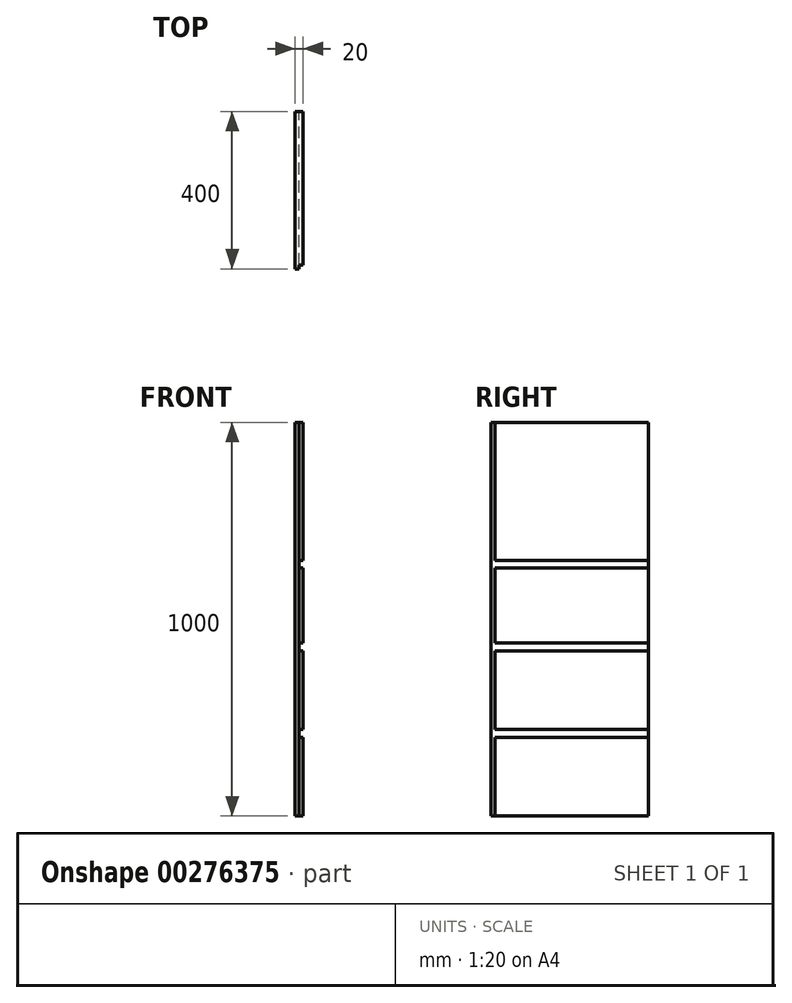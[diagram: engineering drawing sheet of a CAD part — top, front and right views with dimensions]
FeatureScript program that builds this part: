
annotation { "Feature Type Name" : "Feature", "Feature Type Description" : "" }
export const myFeature = defineFeature(function(context is Context, id is Id, definition is map)
    precondition{}
    {
        {
            var Q0;
            Q0=qCreatedBy(makeId("Right.planeOp"),FACE);
            var sketch = newSketch(context, id + "F0", { "sketchPlane" : qUnion([Q0])});
            skLineSegment(sketch, "E0.bottom", {"start": v(-298.33, 493.15) * mm, "end": v(101.67, 493.15) * mm});
            skLineSegment(sketch, "E0.top", {"start": v(-298.33, -506.85) * mm, "end": v(101.67, -506.85) * mm});
            skLineSegment(sketch, "E0.left", {"start": v(-298.33, 493.15) * mm, "end": v(-298.33, -506.85) * mm});
            skLineSegment(sketch, "E0.right", {"start": v(101.67, 493.15) * mm, "end": v(101.67, -506.85) * mm});
            skLineSegment(sketch, "E1", {"start": v(-288.33, 493.15) * mm, "end": v(-288.33, -506.85) * mm});
            skLineSegment(sketch, "E2", {"start": v(-298.33, 143.15) * mm, "end": v(101.67, 143.15) * mm});
            skLineSegment(sketch, "E3", {"start": v(-298.33, 123.15) * mm, "end": v(101.67, 123.15) * mm});
            skLineSegment(sketch, "E4", {"start": v(-298.33, -66.85) * mm, "end": v(101.67, -66.85) * mm});
            skLineSegment(sketch, "E5", {"start": v(-298.33, -86.85) * mm, "end": v(105.13, -86.85) * mm});
            skLineSegment(sketch, "E6", {"start": v(-298.33, -286.85) * mm, "end": v(101.67, -286.85) * mm});
            skLineSegment(sketch, "E7", {"start": v(-298.33, -306.85) * mm, "end": v(101.67, -306.85) * mm});
            skSolve(sketch);
        }
        {
            var Q0;
            {var subQ0=sQuery(id+"F0.wireOp",EDGE,"E0.left");var subQ1=sQuery(id+"F0.wireOp",EDGE,"E0.bottom");var subQ2=makeQuery(id+"F0.imprint","INTERSECT",VERTEX,{"derivedFrom":[subQ1,subQ0]});Q0=makeQuery(id+"F0.imprint","IMPRINT",FACE,{"disambiguationData":[TD([[makeQuery(id+"F0.imprint","IMPRINT",EDGE,{"disambiguationData":[TD([[subQ2,-1.0]])],"derivedFrom":subQ1}),-1.0]])]});}
            var Q1;
            {var subQ0=sQuery(id+"F0.wireOp",EDGE,"E2");var subQ1=sQuery(id+"F0.wireOp",EDGE,"E0.left");var subQ2=makeQuery(id+"F0.imprint","INTERSECT",VERTEX,{"derivedFrom":[subQ1,subQ0]});Q1=makeQuery(id+"F0.imprint","IMPRINT",FACE,{"disambiguationData":[TD([[makeQuery(id+"F0.imprint","IMPRINT",EDGE,{"disambiguationData":[TD([[subQ2,-1.0]])],"derivedFrom":subQ1}),1.0]])]});}
            var Q2;
            {var subQ0=sQuery(id+"F0.wireOp",EDGE,"E3");var subQ1=sQuery(id+"F0.wireOp",EDGE,"E0.left");var subQ2=makeQuery(id+"F0.imprint","INTERSECT",VERTEX,{"derivedFrom":[subQ1,subQ0]});Q2=makeQuery(id+"F0.imprint","IMPRINT",FACE,{"disambiguationData":[TD([[makeQuery(id+"F0.imprint","IMPRINT",EDGE,{"disambiguationData":[TD([[subQ2,-1.0]])],"derivedFrom":subQ1}),1.0]])]});}
            var Q3;
            {var subQ0=sQuery(id+"F0.wireOp",EDGE,"E4");var subQ1=sQuery(id+"F0.wireOp",EDGE,"E0.left");var subQ2=makeQuery(id+"F0.imprint","INTERSECT",VERTEX,{"derivedFrom":[subQ1,subQ0]});Q3=makeQuery(id+"F0.imprint","IMPRINT",FACE,{"disambiguationData":[TD([[makeQuery(id+"F0.imprint","IMPRINT",EDGE,{"disambiguationData":[TD([[subQ2,-1.0]])],"derivedFrom":subQ1}),1.0]])]});}
            var Q4;
            {var subQ0=sQuery(id+"F0.wireOp",EDGE,"E5");var subQ1=sQuery(id+"F0.wireOp",EDGE,"E0.left");var subQ2=makeQuery(id+"F0.imprint","INTERSECT",VERTEX,{"derivedFrom":[subQ1,subQ0]});Q4=makeQuery(id+"F0.imprint","IMPRINT",FACE,{"disambiguationData":[TD([[makeQuery(id+"F0.imprint","IMPRINT",EDGE,{"disambiguationData":[TD([[subQ2,-1.0]])],"derivedFrom":subQ1}),1.0]])]});}
            var Q5;
            {var subQ0=sQuery(id+"F0.wireOp",EDGE,"E2");var subQ1=sQuery(id+"F0.wireOp",EDGE,"E0.right");var subQ2=makeQuery(id+"F0.imprint","INTERSECT",VERTEX,{"derivedFrom":[subQ1,subQ0]});Q5=makeQuery(id+"F0.imprint","IMPRINT",FACE,{"disambiguationData":[TD([[makeQuery(id+"F0.imprint","IMPRINT",EDGE,{"disambiguationData":[TD([[subQ2,-1.0]])],"derivedFrom":subQ1}),-1.0]])]});}
            var Q6;
            {var subQ0=sQuery(id+"F0.wireOp",EDGE,"E4");var subQ1=sQuery(id+"F0.wireOp",EDGE,"E0.right");var subQ2=makeQuery(id+"F0.imprint","INTERSECT",VERTEX,{"derivedFrom":[subQ1,subQ0]});Q6=makeQuery(id+"F0.imprint","IMPRINT",FACE,{"disambiguationData":[TD([[makeQuery(id+"F0.imprint","IMPRINT",EDGE,{"disambiguationData":[TD([[subQ2,-1.0]])],"derivedFrom":subQ1}),-1.0]])]});}
            var Q7;
            {var subQ0=sQuery(id+"F0.wireOp",EDGE,"E6");var subQ1=sQuery(id+"F0.wireOp",EDGE,"E0.right");var subQ2=makeQuery(id+"F0.imprint","INTERSECT",VERTEX,{"derivedFrom":[subQ1,subQ0]});Q7=makeQuery(id+"F0.imprint","IMPRINT",FACE,{"disambiguationData":[TD([[makeQuery(id+"F0.imprint","IMPRINT",EDGE,{"disambiguationData":[TD([[subQ2,-1.0]])],"derivedFrom":subQ1}),-1.0]])]});}
            var Q8;
            {var subQ0=sQuery(id+"F0.wireOp",EDGE,"E6");var subQ1=sQuery(id+"F0.wireOp",EDGE,"E0.left");var subQ2=makeQuery(id+"F0.imprint","INTERSECT",VERTEX,{"derivedFrom":[subQ1,subQ0]});Q8=makeQuery(id+"F0.imprint","IMPRINT",FACE,{"disambiguationData":[TD([[makeQuery(id+"F0.imprint","IMPRINT",EDGE,{"disambiguationData":[TD([[subQ2,-1.0]])],"derivedFrom":subQ1}),1.0]])]});}
            var Q9;
            {var subQ0=sQuery(id+"F0.wireOp",EDGE,"E0.left");var subQ1=sQuery(id+"F0.wireOp",EDGE,"E0.top");var subQ2=makeQuery(id+"F0.imprint","INTERSECT",VERTEX,{"derivedFrom":[subQ1,subQ0]});Q9=makeQuery(id+"F0.imprint","IMPRINT",FACE,{"disambiguationData":[TD([[makeQuery(id+"F0.imprint","IMPRINT",EDGE,{"disambiguationData":[TD([[subQ2,-1.0]])],"derivedFrom":subQ1}),1.0]])]});}
            extrude(context, id + "F1", {"entities" : qUnion([Q0, Q1, Q2, Q3, Q4, Q5, Q6, Q7, Q8, Q9]), "depth" : 10 * mm});
        }
        {
            var Q0;
            {var subQ0=sQuery(id+"F0.wireOp",EDGE,"E0.right");var subQ1=sQuery(id+"F0.wireOp",EDGE,"E0.bottom");var subQ2=makeQuery(id+"F0.imprint","INTERSECT",VERTEX,{"derivedFrom":[subQ1,subQ0]});Q0=makeQuery(id+"F0.imprint","IMPRINT",FACE,{"disambiguationData":[TD([[makeQuery(id+"F0.imprint","IMPRINT",EDGE,{"disambiguationData":[TD([[subQ2,1.0]])],"derivedFrom":subQ1}),-1.0]])]});}
            var Q1;
            {var subQ0=sQuery(id+"F0.wireOp",EDGE,"E3");var subQ1=sQuery(id+"F0.wireOp",EDGE,"E0.right");var subQ2=makeQuery(id+"F0.imprint","INTERSECT",VERTEX,{"derivedFrom":[subQ1,subQ0]});Q1=makeQuery(id+"F0.imprint","IMPRINT",FACE,{"disambiguationData":[TD([[makeQuery(id+"F0.imprint","IMPRINT",EDGE,{"disambiguationData":[TD([[subQ2,-1.0]])],"derivedFrom":subQ1}),-1.0]])]});}
            var Q2;
            {var subQ0=sQuery(id+"F0.wireOp",EDGE,"E6");var subQ1=sQuery(id+"F0.wireOp",EDGE,"E0.right");var subQ2=makeQuery(id+"F0.imprint","INTERSECT",VERTEX,{"derivedFrom":[subQ1,subQ0]});Q2=makeQuery(id+"F0.imprint","IMPRINT",FACE,{"disambiguationData":[TD([[makeQuery(id+"F0.imprint","IMPRINT",EDGE,{"disambiguationData":[TD([[subQ2,1.0]])],"derivedFrom":subQ1}),-1.0]])]});}
            var Q3;
            {var subQ0=sQuery(id+"F0.wireOp",EDGE,"E0.right");var subQ1=sQuery(id+"F0.wireOp",EDGE,"E0.top");var subQ2=makeQuery(id+"F0.imprint","INTERSECT",VERTEX,{"derivedFrom":[subQ1,subQ0]});Q3=makeQuery(id+"F0.imprint","IMPRINT",FACE,{"disambiguationData":[TD([[makeQuery(id+"F0.imprint","IMPRINT",EDGE,{"disambiguationData":[TD([[subQ2,1.0]])],"derivedFrom":subQ1}),1.0]])]});}
            extrude(context, id + "F2", {"entities" : qUnion([Q0, Q1, Q2, Q3]), "operationType" : NewBodyOperationType.ADD, "depth" : 20 * mm});
        }
    });
